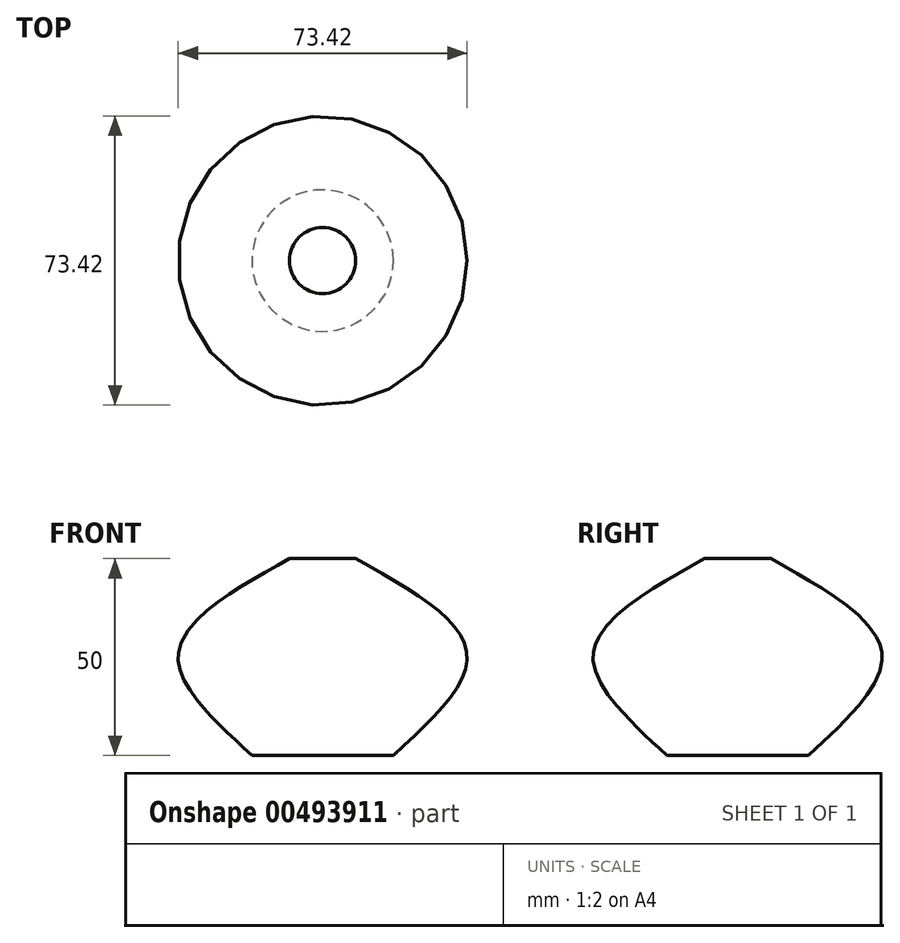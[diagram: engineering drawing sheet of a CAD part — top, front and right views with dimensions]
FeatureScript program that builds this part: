
annotation { "Feature Type Name" : "Feature", "Feature Type Description" : "" }
export const myFeature = defineFeature(function(context is Context, id is Id, definition is map)
    precondition{}
    {
        {
            var Q0;
            Q0=qCreatedBy(makeId("Top.planeOp"),FACE);
            cPlane(context, id + "F0", {"entities" : qUnion([Q0]), "cplaneType" : CPlaneType.OFFSET, "offset" : 25 * mm, "width" : 150 * mm, "height" : 150 * mm});
        }
        {
            var Q0;
            Q0=qCreatedBy(id+"F0.planeOp",FACE);
            cPlane(context, id + "F1", {"entities" : qUnion([Q0]), "cplaneType" : CPlaneType.OFFSET, "offset" : 25 * mm, "width" : 150 * mm, "height" : 150 * mm});
        }
        {
            var Q0;
            Q0=qCreatedBy(makeId("Top.planeOp"),FACE);
            var sketch = newSketch(context, id + "F2", { "sketchPlane" : qUnion([Q0])});
            skCircle(sketch, "E0", {"center": v(0, 0) * mm, "radius": 17.96 * mm});
            skSolve(sketch);
        }
        {
            var Q0;
            Q0=qCreatedBy(id+"F0.planeOp",FACE);
            var sketch = newSketch(context, id + "F3", { "sketchPlane" : qUnion([Q0])});
            skCircle(sketch, "E1", {"center": v(0, 0) * mm, "radius": 36.7 * mm});
            skSolve(sketch);
        }
        {
            var Q0;
            Q0=qCreatedBy(id+"F1.planeOp",FACE);
            var sketch = newSketch(context, id + "F4", { "sketchPlane" : qUnion([Q0])});
            skCircle(sketch, "E2", {"center": v(0, 0) * mm, "radius": 8.42 * mm});
            skSolve(sketch);
        }
        {
            var Q0;
            Q0=makeQuery(id+"F2.imprint","IMPRINT",FACE,{"disambiguationData":[TD([[makeQuery(id+"F2.imprint","IMPRINT",EDGE,{"derivedFrom":sQuery(id+"F2.wireOp",EDGE,"E0")}),1.0]])]});
            var Q1;
            Q1=makeQuery(id+"F3.imprint","IMPRINT",FACE,{"disambiguationData":[TD([[makeQuery(id+"F3.imprint","IMPRINT",EDGE,{"derivedFrom":sQuery(id+"F3.wireOp",EDGE,"E1")}),1.0]])]});
            var Q2;
            Q2=makeQuery(id+"F4.imprint","IMPRINT",FACE,{"disambiguationData":[TD([[makeQuery(id+"F4.imprint","IMPRINT",EDGE,{"derivedFrom":sQuery(id+"F4.wireOp",EDGE,"E2")}),1.0]])]});
            loft(context, id + "F5", {"sheetProfilesArray" : [{ "sheetProfileEntities" : qUnion([Q0]) }, { "sheetProfileEntities" : qUnion([Q1]) }, { "sheetProfileEntities" : qUnion([Q2]) }]});
        }
    });
